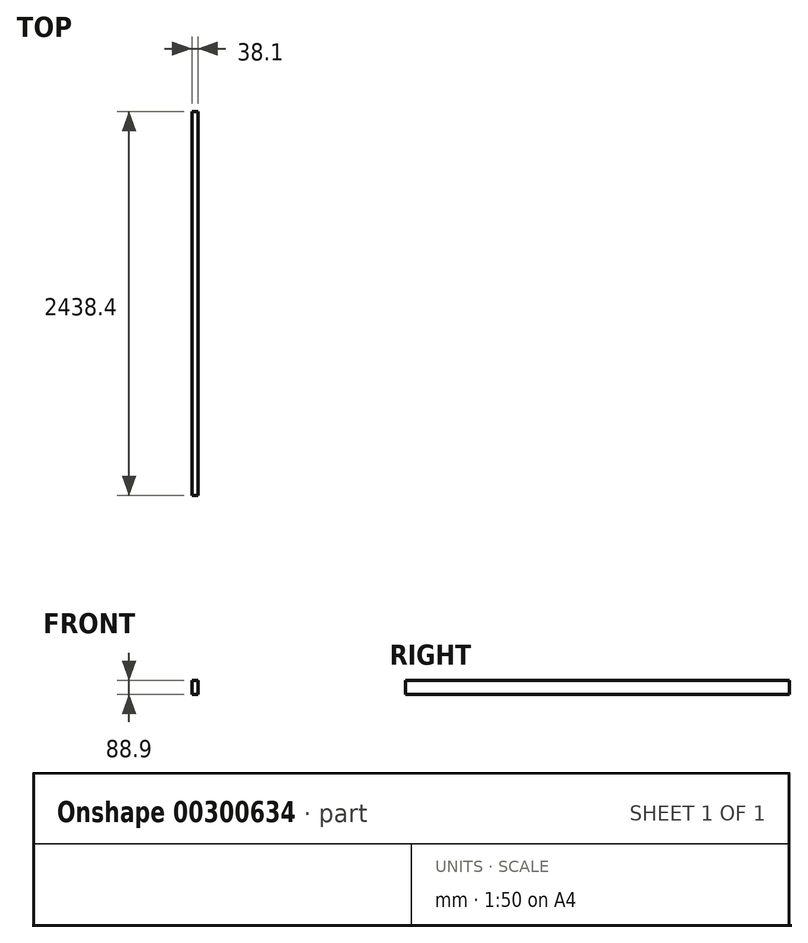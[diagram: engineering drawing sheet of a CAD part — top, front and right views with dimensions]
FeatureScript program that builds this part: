
annotation { "Feature Type Name" : "Feature", "Feature Type Description" : "" }
export const myFeature = defineFeature(function(context is Context, id is Id, definition is map)
    precondition{}
    {
        {
            var Q0;
            Q0=qCreatedBy(makeId("Front.planeOp"),FACE);
            var sketch = newSketch(context, id + "F0", { "sketchPlane" : qUnion([Q0])});
            skLineSegment(sketch, "E0.bottom", {"start": v(19.05, 44.45) * mm, "end": v(-19.05, 44.45) * mm});
            skLineSegment(sketch, "E0.top", {"start": v(19.05, -44.45) * mm, "end": v(-19.05, -44.45) * mm});
            skLineSegment(sketch, "E0.left", {"start": v(19.05, 44.45) * mm, "end": v(19.05, -44.45) * mm});
            skLineSegment(sketch, "E0.right", {"start": v(-19.05, 44.45) * mm, "end": v(-19.05, -44.45) * mm});
            skPoint(sketch, "E0.middle", {"position": v(0, 0) * mm});
            skSolve(sketch);
        }
        {
            var Q0;
            Q0 = qSketchRegion(id + "F0", true);
            extrude(context, id + "F1", {"entities" : qUnion([Q0]), "oppositeDirection" : true, "depth" : 2438.4 * mm});
        }
    });
